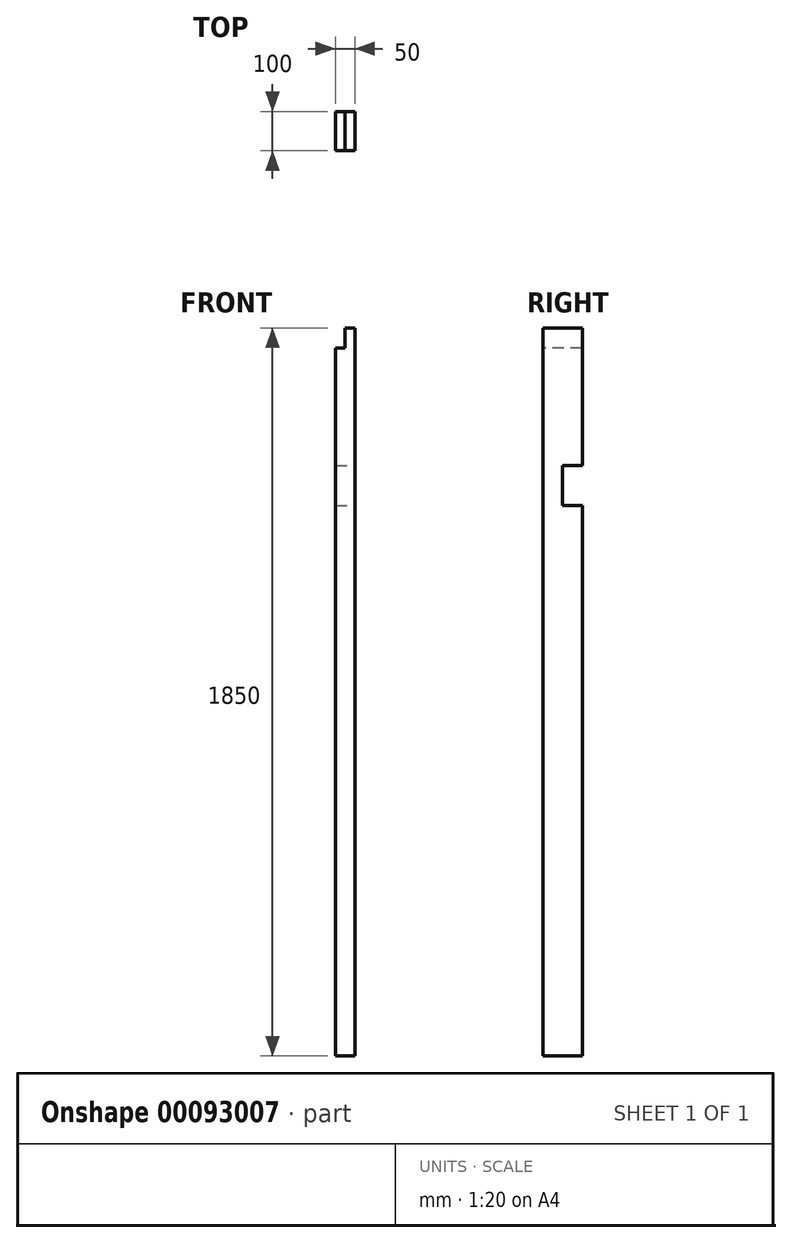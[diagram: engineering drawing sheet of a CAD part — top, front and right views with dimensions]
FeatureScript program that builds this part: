
annotation { "Feature Type Name" : "Feature", "Feature Type Description" : "" }
export const myFeature = defineFeature(function(context is Context, id is Id, definition is map)
    precondition{}
    {
        {
            var Q0;
            Q0=qCreatedBy(makeId("Top.planeOp"),FACE);
            var sketch = newSketch(context, id + "F0", { "sketchPlane" : qUnion([Q0])});
            skLineSegment(sketch, "E0.bottom", {"start": v(25, 50) * mm, "end": v(-25, 50) * mm});
            skLineSegment(sketch, "E0.top", {"start": v(25, -50) * mm, "end": v(-25, -50) * mm});
            skLineSegment(sketch, "E0.left", {"start": v(25, 50) * mm, "end": v(25, -50) * mm});
            skLineSegment(sketch, "E0.right", {"start": v(-25, 50) * mm, "end": v(-25, -50) * mm});
            skPoint(sketch, "E0.middle", {"position": v(0, 0) * mm});
            skSolve(sketch);
        }
        {
            var Q0;
            Q0=makeQuery(id+"F0.imprint","IMPRINT",FACE,{"disambiguationData":[TD([[makeQuery(id+"F0.imprint","IMPRINT",EDGE,{"derivedFrom":sQuery(id+"F0.wireOp",EDGE,"E0.bottom")}),1.0]])]});
            extrude(context, id + "F1", {"entities" : qUnion([Q0]), "depth" : 1850 * mm});
        }
        {
            var Q0;
            Q0=qCreatedBy(makeId("Right.planeOp"),FACE);
            var sketch = newSketch(context, id + "F2", { "sketchPlane" : qUnion([Q0])});
            skLineSegment(sketch, "E1.bottom", {"start": v(-0.8, 1500) * mm, "end": v(50, 1500) * mm});
            skLineSegment(sketch, "E1.top", {"start": v(-0.8, 1398.4) * mm, "end": v(50, 1398.4) * mm});
            skLineSegment(sketch, "E1.left", {"start": v(-0.8, 1500) * mm, "end": v(-0.8, 1398.4) * mm});
            skLineSegment(sketch, "E1.right", {"start": v(50, 1500) * mm, "end": v(50, 1398.4) * mm});
            skSolve(sketch);
        }
        {
            var Q0;
            Q0=qSketchRegion(id+"F2",true);
            extrude(context, id + "F3", {"entities" : qUnion([Q0]), "operationType" : NewBodyOperationType.REMOVE, "endBound" : BoundingType.SYMMETRIC, "oppositeDirection" : true, "depth" : 100 * mm});
        }
        {
            var Q0;
            Q0=makeQuery(id+"F1.opExtrude","CAP_FACE",FACE,{"disambiguationData":[OSD([sQuery(id+"F0.wireOp",EDGE,"E0.bottom"),sQuery(id+"F0.wireOp",EDGE,"E0.top"),sQuery(id+"F0.wireOp",EDGE,"E0.left"),sQuery(id+"F0.wireOp",EDGE,"E0.right")])],"isStart":false});
            var sketch = newSketch(context, id + "F4", { "sketchPlane" : qUnion([Q0])});
            skLineSegment(sketch, "E2.bottom", {"start": v(-25, -50) * mm, "end": v(0, -50) * mm});
            skLineSegment(sketch, "E2.top", {"start": v(-25, 50) * mm, "end": v(0, 50) * mm});
            skLineSegment(sketch, "E2.left", {"start": v(-25, -50) * mm, "end": v(-25, 50) * mm});
            skLineSegment(sketch, "E2.right", {"start": v(0, -50) * mm, "end": v(0, 50) * mm});
            skSolve(sketch);
        }
        {
            var Q0;
            Q0=makeQuery(id+"F4.imprint","IMPRINT",FACE,{"disambiguationData":[TD([[makeQuery(id+"F4.imprint","IMPRINT",EDGE,{"derivedFrom":sQuery(id+"F4.wireOp",EDGE,"fYNU90H2-l5nf-3GHt-qqRk-XDixcM1YwMOO.bottom")}),1.0]])]});
            var Q1;
            Q1=makeQuery(id+"F4.imprint","IMPRINT",FACE,{"disambiguationData":[TD([[makeQuery(id+"F4.imprint","IMPRINT",EDGE,{"derivedFrom":sQuery(id+"F4.wireOp",EDGE,"E2.bottom")}),-1.0]])]});
            extrude(context, id + "F5", {"entities" : qUnion([Q0, Q1]), "operationType" : NewBodyOperationType.REMOVE, "oppositeDirection" : true, "depth" : 50.8 * mm});
        }
    });
